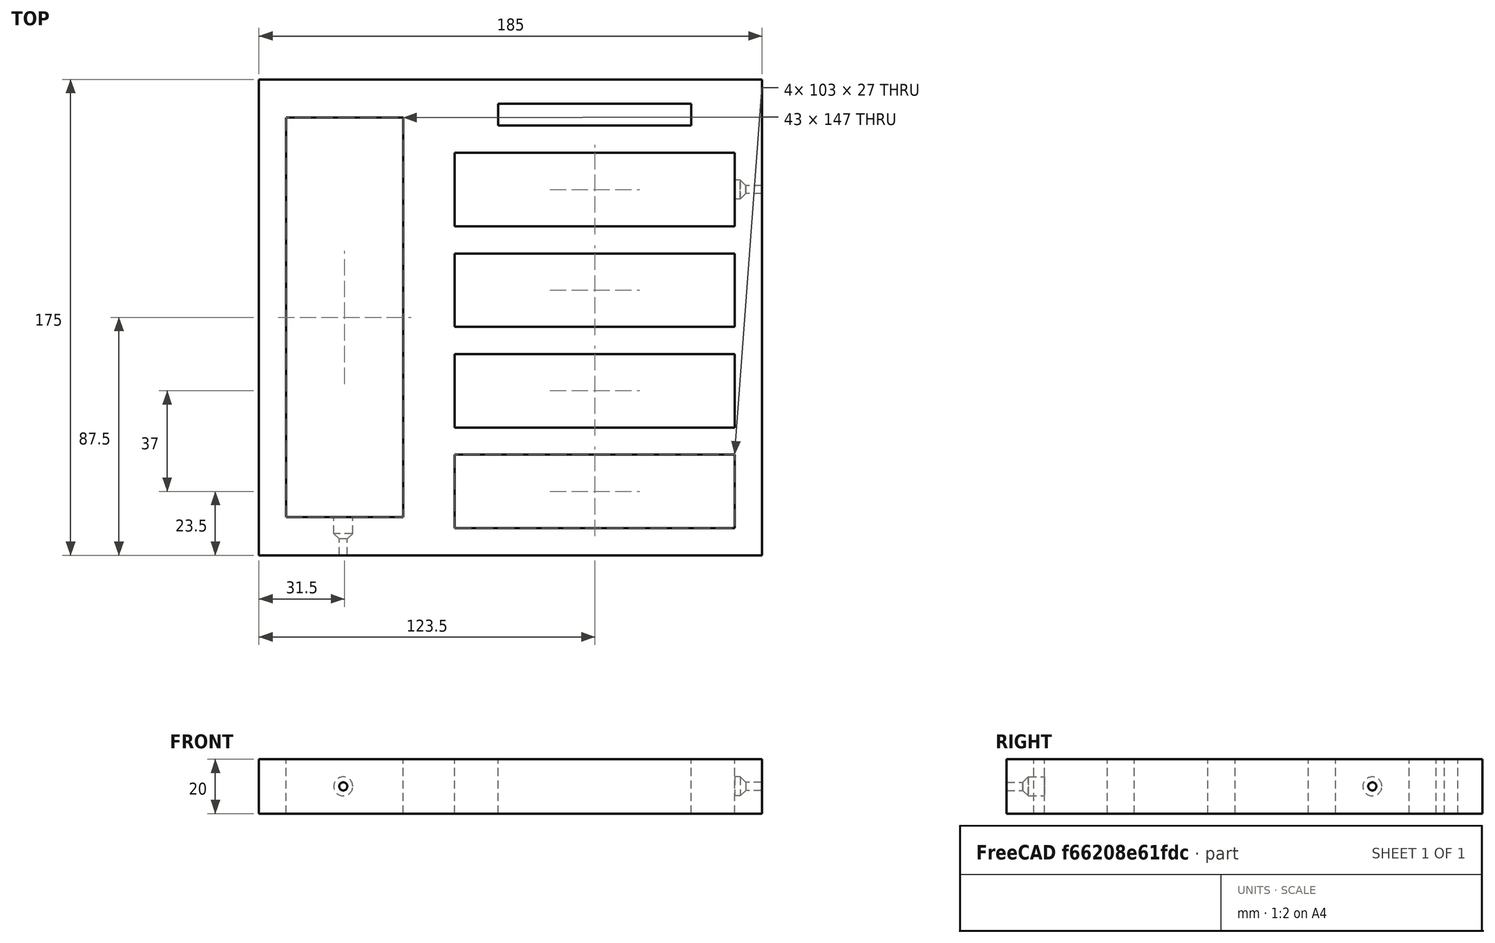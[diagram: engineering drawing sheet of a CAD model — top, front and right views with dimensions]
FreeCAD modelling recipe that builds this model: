
FCSTD DOCUMENT  (FreeCAD 0.16R6703 (Git))
Label: Soporte Discos y CD
License: All rights reserved
LicenseURL: http://en.wikipedia.org/wiki/All_rights_reserved
objects: Part::Box×4, Part::MultiFuse×3, Part::Cylinder×2, Part::FeaturePython×1, Part::Cone×1, Part::Cut×1
note: 12 computed .brp shape members not serialized (recipe doc carries the construction recipe); baked Part::Feature solids carry a one-line shape summary decoded from their .brp

FEATURE [Part::Box] Box  label="Cube"
  Height = 146
  Length = 103
  Width = 27
FEATURE [Part::FeaturePython] Array  # Draft array (typed FeaturePython)
  Angle = 360
  ArrayType = 0
  Axis = (0,0,1)
  Base = -> Box
  Center = (0,0,0)
  Fuse = false
  IntervalAxis = (0,0,0)
  IntervalX = (1,0,0)
  IntervalY = (0,37,0)
  IntervalZ = (0,0,0)
  NumberPolar = 1
  NumberX = 1
  NumberY = 4
  NumberZ = 1
FEATURE [Part::Box] Box001  label="Cube001"
  Height = 100
  Length = 71
  Placement = pos=(16,148,0) rot=(0,0,1;0rad)
  Width = 8
FEATURE [Part::Box] Box002  label="Cube002"
  Height = 20
  Length = 185
  Placement = pos=(-72,-10,0) rot=(0,0,1;0rad)
  Width = 175
FEATURE [Part::Cylinder] Cylinder001
  Angle = 360
  Height = 10
  Placement = pos=(15,-5,0) rot=(0,0,1;0rad)
  Radius = 1.5
FEATURE [Part::Cylinder] Cylinder002
  Angle = 360
  Height = 10
  Placement = pos=(15,-5,8) rot=(0,0,1;0rad)
  Radius = 3.5
FEATURE [Part::Cone] Cone
  Angle = 360
  Height = 2
  Placement = pos=(15,-5,6) rot=(0,0,1;0rad)
  Radius1 = 1.5
  Radius2 = 3.5
FEATURE [Part::MultiFuse] Fusion001
  Placement = pos=(113,129.5,-5) rot=(0,-1,0;1.5708rad)
  Shapes = -> [Cylinder001,Cylinder002,Cone]
FEATURE [Part::MultiFuse] Fusion002
  Placement = pos=(-56,-10,5) rot=(-1,0,0;1.5708rad)
  Shapes = -> [Cylinder001,Cylinder002,Cone]
FEATURE [Part::Box] Box005  label="Cube005"
  Height = 20
  Length = 43
  Placement = pos=(-62,4,0) rot=(0,0,1;0rad)
  Width = 147
FEATURE [Part::MultiFuse] Fusion
  Shapes = -> [Box005,Fusion002,Fusion001,Box001,Array]
FEATURE [Part::Cut] Cut
  Base = -> Box002
  Tool = -> Fusion
